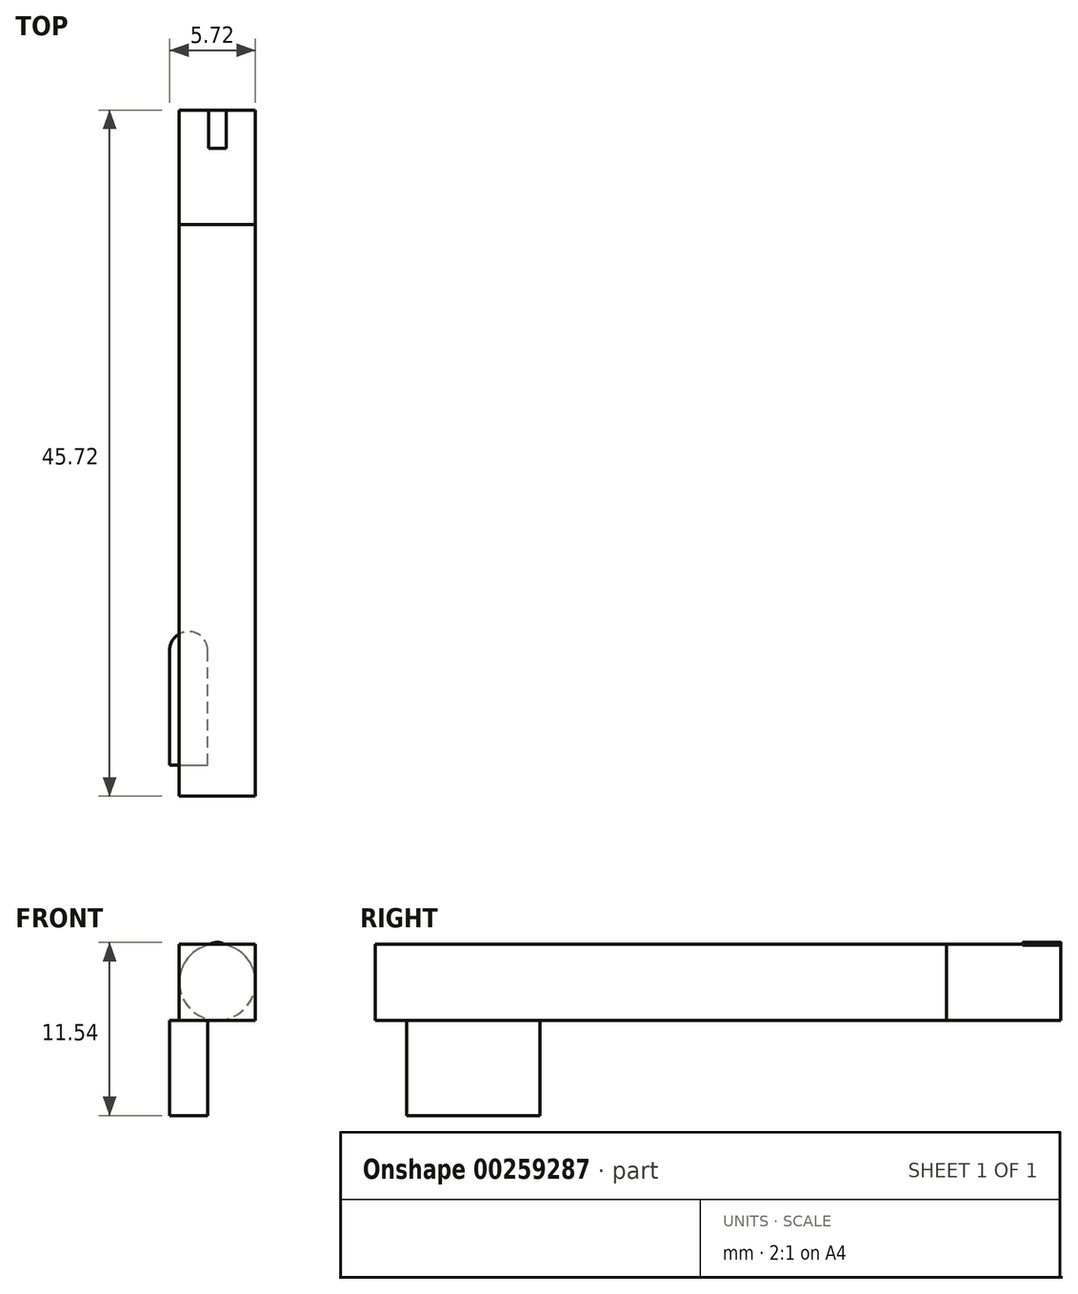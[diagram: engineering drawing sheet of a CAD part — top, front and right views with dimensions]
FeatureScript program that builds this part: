
annotation { "Feature Type Name" : "Feature", "Feature Type Description" : "" }
export const myFeature = defineFeature(function(context is Context, id is Id, definition is map)
    precondition{}
    {
        {
            var Q0;
            Q0=qCreatedBy(makeId("Front.planeOp"),FACE);
            var sketch = newSketch(context, id + "F0", { "sketchPlane" : qUnion([Q0])});
            skLineSegment(sketch, "E0.bottom", {"start": v(2.54, 2.54) * mm, "end": v(-2.54, 2.54) * mm});
            skLineSegment(sketch, "E0.top", {"start": v(2.54, -2.54) * mm, "end": v(-2.54, -2.54) * mm});
            skLineSegment(sketch, "E0.left", {"start": v(2.54, 2.54) * mm, "end": v(2.54, -2.54) * mm});
            skLineSegment(sketch, "E0.right", {"start": v(-2.54, 2.54) * mm, "end": v(-2.54, -2.54) * mm});
            skPoint(sketch, "E0.middle", {"position": v(0, 0) * mm});
            skSolve(sketch);
        }
        {
            var Q0;
            Q0 = qSketchRegion(id + "F0", true);
            extrude(context, id + "F1", {"entities" : qUnion([Q0]), "depth" : 25.4 * mm});
        }
        {
            var Q0;
            Q0=makeQuery(id+"F1.opExtrude","SWEPT_FACE",FACE,{"disambiguationData":[OSD([sQuery(id+"F0.wireOp",EDGE,"E0.top")])]});
            var sketch = newSketch(context, id + "F2", { "sketchPlane" : qUnion([Q0])});
            skLineSegment(sketch, "E1.bottom", {"start": v(-3.18, 23.32) * mm, "end": v(-0.64, 23.32) * mm});
            skLineSegment(sketch, "E1.top", {"start": v(-3.18, 15.7) * mm, "end": v(-0.64, 15.7) * mm});
            skLineSegment(sketch, "E1.left", {"start": v(-3.18, 23.32) * mm, "end": v(-3.18, 15.7) * mm});
            skLineSegment(sketch, "E1.right", {"start": v(-0.64, 23.32) * mm, "end": v(-0.64, 15.7) * mm});
            skLineSegment(sketch, "E2", {"start": v(-3.18, 19.51) * mm, "end": v(-2.54, 19.51) * mm, "construction": true});
            skLineSegment(sketch, "E3", {"start": v(2.54, 19.51) * mm, "end": v(-0.64, 19.51) * mm, "construction": true});
            skArc(sketch, "E4", {"start": v(-3.18, 15.7) * mm, "mid": v(-1.91, 14.43) * mm, "end": v(-0.64, 15.7) * mm});
            skSolve(sketch);
        }
        {
            var Q0;
            Q0 = qSketchRegion(id + "F2", true);
            extrude(context, id + "F3", {"entities" : qUnion([Q0]), "operationType" : NewBodyOperationType.ADD, "depth" : 6.35 * mm});
        }
        {
            var Q0;
            Q0=makeQuery(id+"F1.opExtrude","CAP_FACE",FACE,{"disambiguationData":[OSD([sQuery(id+"F0.wireOp",EDGE,"E0.bottom"),sQuery(id+"F0.wireOp",EDGE,"E0.top"),sQuery(id+"F0.wireOp",EDGE,"E0.left"),sQuery(id+"F0.wireOp",EDGE,"E0.right")])],"isStart":true});
            extrude(context, id + "F4", {"entities" : qUnion([Q0]), "operationType" : NewBodyOperationType.ADD, "depth" : 12.7 * mm});
        }
        {
            var Q0;
            Q0=makeQuery(id+"F4.opExtrude","CAP_FACE",FACE,{"disambiguationData":[OSD([sQuery(id+"F0.wireOp",EDGE,"E0.bottom"),sQuery(id+"F0.wireOp",EDGE,"E0.top"),sQuery(id+"F0.wireOp",EDGE,"E0.left"),sQuery(id+"F0.wireOp",EDGE,"E0.right")])],"isStart":false});
            var sketch = newSketch(context, id + "F5", { "sketchPlane" : qUnion([Q0])});
            skPoint(sketch, "E5.endSnap0", {"position": v(0, -2.54) * mm});
            skCircle(sketch, "E6", {"center": v(0, 0) * mm, "radius": 2.54 * mm});
            skSolve(sketch);
        }
        {
            var Q0;
            {var subQ0=sQuery(id+"F5.wireOp",EDGE,"E6");var subQ1=makeQuery(id+"F5.imprint","INTERSECT",VERTEX,{"derivedFrom":[makeQuery(id+"F4.opExtrude","CAP_EDGE",EDGE,{"disambiguationData":[OSD([sQuery(id+"F0.wireOp",EDGE,"E0.bottom")])],"isStart":false}),subQ0]});Q0=makeQuery(id+"F5.imprint","IMPRINT",FACE,{"disambiguationData":[TD([[makeQuery(id+"F5.imprint","IMPRINT",EDGE,{"disambiguationData":[TD([[subQ1,1.0]])],"derivedFrom":subQ0}),1.0]])]});}
            extrude(context, id + "F6", {"entities" : qUnion([Q0]), "operationType" : NewBodyOperationType.ADD, "depth" : 7.62 * mm});
        }
        {
            var Q0;
            Q0=makeQuery(id+"F6.opExtrude","CAP_FACE",FACE,{"disambiguationData":[OSD([sQuery(id+"F5.wireOp",EDGE,"E6")])],"isStart":false});
            var sketch = newSketch(context, id + "F7", { "sketchPlane" : qUnion([Q0])});
            skLineSegment(sketch, "E7", {"start": v(0, 0) * mm, "end": v(0, 2.54) * mm, "construction": true});
            skLineSegment(sketch, "E8", {"start": v(0, 0) * mm, "end": v(-0.6, 2.47) * mm});
            skLineSegment(sketch, "E9", {"start": v(0, 0) * mm, "end": v(0.6, 2.47) * mm});
            skArc(sketch, "E10", {"start": v(0.6, 2.47) * mm, "mid": v(0, 2.65) * mm, "end": v(-0.6, 2.47) * mm});
            skSolve(sketch);
        }
        {
            var Q0;
            {var subQ0=sQuery(id+"F7.wireOp",EDGE,"E10");Q0=makeQuery(id+"F7.imprint","IMPRINT",FACE,{"disambiguationData":[TD([[makeQuery(id+"F7.imprint","IMPRINT",EDGE,{"derivedFrom":subQ0}),1.0]])]});}
            extrude(context, id + "F8", {"entities" : qUnion([Q0]), "operationType" : NewBodyOperationType.ADD, "oppositeDirection" : true, "depth" : 2.54 * mm});
        }
    });
